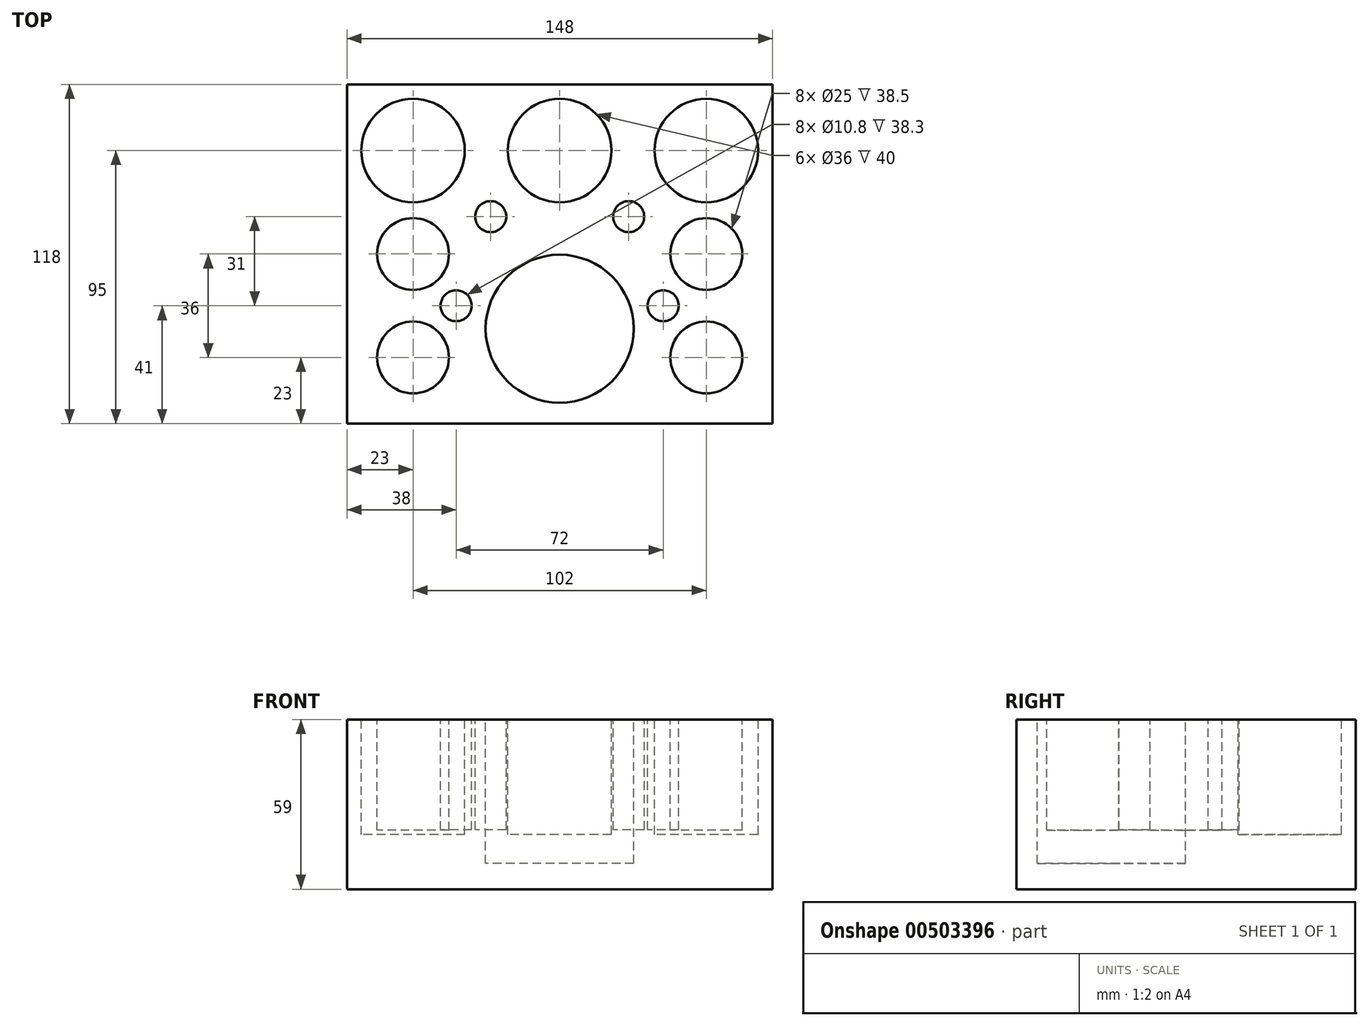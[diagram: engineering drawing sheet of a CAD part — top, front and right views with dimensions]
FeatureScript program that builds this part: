
annotation { "Feature Type Name" : "Feature", "Feature Type Description" : "" }
export const myFeature = defineFeature(function(context is Context, id is Id, definition is map)
    precondition{}
    {
        {
            var Q0;
            Q0=qCreatedBy(makeId("Top.planeOp"),FACE);
            var sketch = newSketch(context, id + "F0", { "sketchPlane" : qUnion([Q0])});
            skLineSegment(sketch, "E0.bottom", {"start": v(74, -59) * mm, "end": v(-74, -59) * mm});
            skLineSegment(sketch, "E0.top", {"start": v(74, 59) * mm, "end": v(-74, 59) * mm});
            skLineSegment(sketch, "E0.left", {"start": v(74, -59) * mm, "end": v(74, 59) * mm});
            skLineSegment(sketch, "E0.right", {"start": v(-74, -59) * mm, "end": v(-74, 59) * mm});
            skPoint(sketch, "E0.middle", {"position": v(0, 0) * mm});
            skSolve(sketch);
        }
        {
            var Q0;
            Q0 = qSketchRegion(id + "F0", true);
            extrude(context, id + "F1", {"entities" : qUnion([Q0]), "depth" : 59 * mm, "offsetDistance" : 25 * mm});
        }
        {
            var Q0;
            Q0=makeQuery(id+"F1.opExtrude","CAP_FACE",FACE,{"disambiguationData":[OSD([sQuery(id+"F0.wireOp",EDGE,"E0.bottom"),sQuery(id+"F0.wireOp",EDGE,"E0.top"),sQuery(id+"F0.wireOp",EDGE,"E0.left"),sQuery(id+"F0.wireOp",EDGE,"E0.right")])],"isStart":false});
            var sketch = newSketch(context, id + "F2", { "sketchPlane" : qUnion([Q0])});
            skPoint(sketch, "E1.middle", {"position": v(0, 0) * mm});
            skCircle(sketch, "E2", {"center": v(-51, 36) * mm, "radius": 18 * mm});
            skCircle(sketch, "E3", {"center": v(51, 36) * mm, "radius": 18 * mm});
            skCircle(sketch, "E4", {"center": v(51, -36) * mm, "radius": 12.5 * mm});
            skCircle(sketch, "E5", {"center": v(-51, -36) * mm, "radius": 12.5 * mm});
            skCircle(sketch, "E6", {"center": v(-51, 0) * mm, "radius": 12.5 * mm});
            skCircle(sketch, "E7", {"center": v(51, 0) * mm, "radius": 12.5 * mm});
            skCircle(sketch, "E8", {"center": v(0, 36) * mm, "radius": 18 * mm});
            skCircle(sketch, "E9", {"center": v(-36, -18) * mm, "radius": 5.4 * mm});
            skCircle(sketch, "E10", {"center": v(-24, 13) * mm, "radius": 5.4 * mm});
            skCircle(sketch, "E11", {"center": v(24, 13) * mm, "radius": 5.4 * mm});
            skCircle(sketch, "E12", {"center": v(36, -18) * mm, "radius": 5.4 * mm});
            skCircle(sketch, "E13", {"center": v(0, -26) * mm, "radius": 25.75 * mm});
            skSolve(sketch);
        }
        {
            var Q0;
            Q0=makeQuery(id+"F2.imprint","IMPRINT",FACE,{"disambiguationData":[TD([[makeQuery(id+"F2.imprint","IMPRINT",EDGE,{"derivedFrom":sQuery(id+"F2.wireOp",EDGE,"E13")}),1.0]])]});
            var Q1;
            Q1=sQuery(id+"F2.wireOp",EDGE,"PrFnkiJH-hDgl-UGHf-EqaK-b7aYafvgXTId");
            extrude(context, id + "F3", {"entities" : qUnion([Q0]), "operationType" : NewBodyOperationType.REMOVE, "surfaceEntities" : qUnion([Q1]), "oppositeDirection" : true, "depth" : 50 * mm, "offsetDistance" : 25 * mm});
        }
        {
            var Q0;
            Q0=makeQuery(id+"F2.imprint","IMPRINT",FACE,{"disambiguationData":[TD([[makeQuery(id+"F2.imprint","IMPRINT",EDGE,{"derivedFrom":sQuery(id+"F2.wireOp",EDGE,"E2")}),1.0]])]});
            var Q1;
            Q1=makeQuery(id+"F2.imprint","IMPRINT",FACE,{"disambiguationData":[TD([[makeQuery(id+"F2.imprint","IMPRINT",EDGE,{"derivedFrom":sQuery(id+"F2.wireOp",EDGE,"E8")}),1.0]])]});
            var Q2;
            Q2=makeQuery(id+"F2.imprint","IMPRINT",FACE,{"disambiguationData":[TD([[makeQuery(id+"F2.imprint","IMPRINT",EDGE,{"derivedFrom":sQuery(id+"F2.wireOp",EDGE,"E3")}),1.0]])]});
            extrude(context, id + "F4", {"entities" : qUnion([Q0, Q1, Q2]), "operationType" : NewBodyOperationType.REMOVE, "oppositeDirection" : true, "depth" : 40 * mm, "offsetDistance" : 25 * mm});
        }
        {
            var Q0;
            Q0=makeQuery(id+"F2.imprint","IMPRINT",FACE,{"disambiguationData":[TD([[makeQuery(id+"F2.imprint","IMPRINT",EDGE,{"derivedFrom":sQuery(id+"F2.wireOp",EDGE,"E6")}),1.0]])]});
            var Q1;
            Q1=makeQuery(id+"F2.imprint","IMPRINT",FACE,{"disambiguationData":[TD([[makeQuery(id+"F2.imprint","IMPRINT",EDGE,{"derivedFrom":sQuery(id+"F2.wireOp",EDGE,"E5")}),1.0]])]});
            var Q2;
            Q2=makeQuery(id+"F2.imprint","IMPRINT",FACE,{"disambiguationData":[TD([[makeQuery(id+"F2.imprint","IMPRINT",EDGE,{"derivedFrom":sQuery(id+"F2.wireOp",EDGE,"E7")}),1.0]])]});
            var Q3;
            Q3=makeQuery(id+"F2.imprint","IMPRINT",FACE,{"disambiguationData":[TD([[makeQuery(id+"F2.imprint","IMPRINT",EDGE,{"derivedFrom":sQuery(id+"F2.wireOp",EDGE,"E4")}),1.0]])]});
            extrude(context, id + "F5", {"entities" : qUnion([Q0, Q1, Q2, Q3]), "operationType" : NewBodyOperationType.REMOVE, "oppositeDirection" : true, "depth" : 38.5 * mm, "offsetDistance" : 25 * mm});
        }
        {
            var Q0;
            Q0=makeQuery(id+"F2.imprint","IMPRINT",FACE,{"disambiguationData":[TD([[makeQuery(id+"F2.imprint","IMPRINT",EDGE,{"derivedFrom":sQuery(id+"F2.wireOp",EDGE,"E10")}),1.0]])]});
            var Q1;
            Q1=makeQuery(id+"F2.imprint","IMPRINT",FACE,{"disambiguationData":[TD([[makeQuery(id+"F2.imprint","IMPRINT",EDGE,{"derivedFrom":sQuery(id+"F2.wireOp",EDGE,"E9")}),1.0]])]});
            var Q2;
            Q2=makeQuery(id+"F2.imprint","IMPRINT",FACE,{"disambiguationData":[TD([[makeQuery(id+"F2.imprint","IMPRINT",EDGE,{"derivedFrom":sQuery(id+"F2.wireOp",EDGE,"E11")}),1.0]])]});
            var Q3;
            Q3=makeQuery(id+"F2.imprint","IMPRINT",FACE,{"disambiguationData":[TD([[makeQuery(id+"F2.imprint","IMPRINT",EDGE,{"derivedFrom":sQuery(id+"F2.wireOp",EDGE,"E12")}),1.0]])]});
            extrude(context, id + "F6", {"entities" : qUnion([Q0, Q1, Q2, Q3]), "operationType" : NewBodyOperationType.REMOVE, "oppositeDirection" : true, "depth" : 38.3 * mm, "offsetDistance" : 25 * mm});
        }
    });
